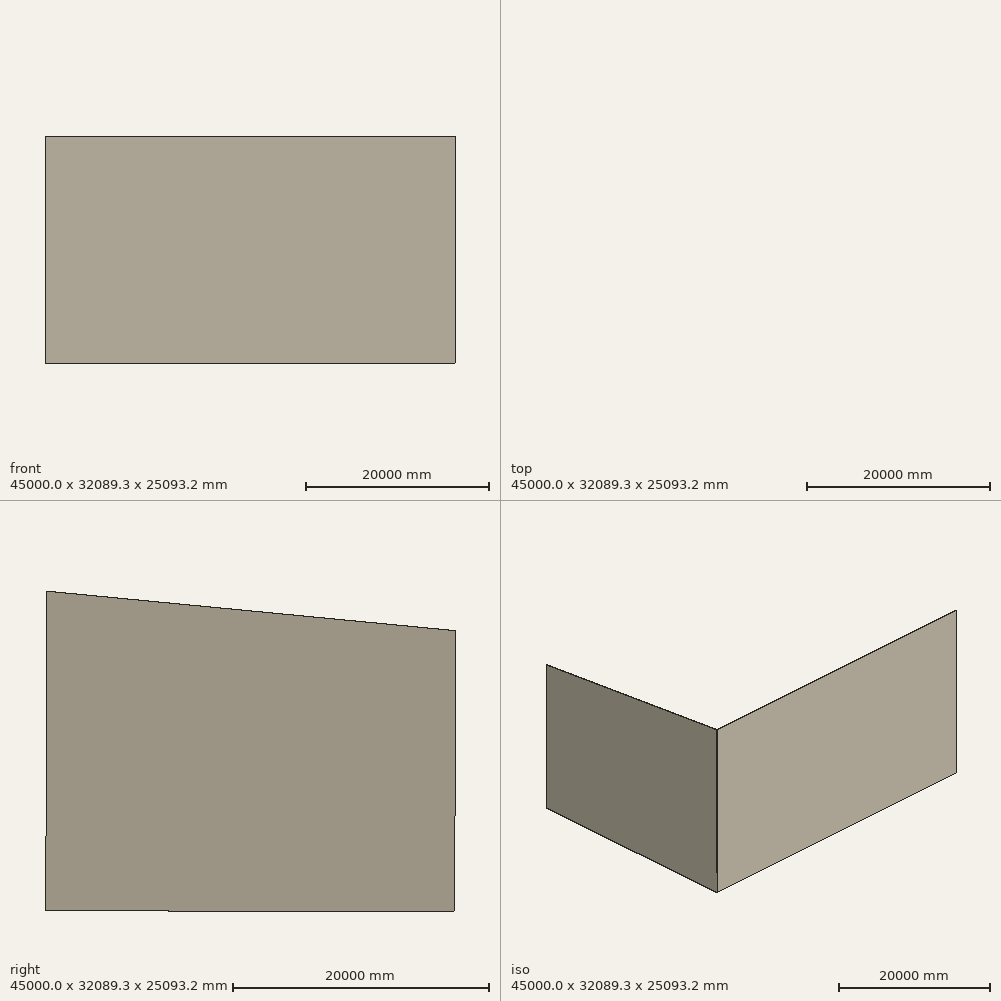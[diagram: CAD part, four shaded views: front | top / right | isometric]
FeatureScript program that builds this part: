
annotation { "Feature Type Name" : "Feature", "Feature Type Description" : "" }
export const myFeature = defineFeature(function(context is Context, id is Id, definition is map)
    precondition{}
    {
        {
            var Q0;
            Q0=qCreatedBy(makeId("Front.planeOp"),FACE);
            var sketch = newSketch(context, id + "F0", { "sketchPlane" : qUnion([Q0])});
            skLineSegment(sketch, "E0.bottom", {"start": v(0, 0) * mm, "end": v(45000, 0) * mm});
            skLineSegment(sketch, "E0.top", {"start": v(0, 25000) * mm, "end": v(45000, 25000) * mm});
            skLineSegment(sketch, "E0.left", {"start": v(0, 0) * mm, "end": v(0, 25000) * mm});
            skLineSegment(sketch, "E0.right", {"start": v(45000, 0) * mm, "end": v(45000, 25000) * mm});
            skSolve(sketch);
        }
        {
            var Q0;
            Q0 = qSketchRegion(id + "F0", true);
            extrude(context, id + "F1", {"entities" : qUnion([Q0]), "depth" : 25.4 * mm, "offsetDistance" : 25.4 * mm});
        }
        {
            var Q0;
            Q0=qCreatedBy(makeId("Right.planeOp"),FACE);
            var sketch = newSketch(context, id + "F2", { "sketchPlane" : qUnion([Q0])});
            skLineSegment(sketch, "E1", {"start": v(0, 0) * mm, "end": v(31999.86, -93.2) * mm});
            skLineSegment(sketch, "E2", {"start": v(31999.86, -93.2) * mm, "end": v(32063.93, 21906.72) * mm});
            skLineSegment(sketch, "E3", {"start": v(32063.93, 21906.72) * mm, "end": v(72.8, 24999.9) * mm});
            skLineSegment(sketch, "E4", {"start": v(72.8, 24999.9) * mm, "end": v(0, 0) * mm});
            skSolve(sketch);
        }
        {
            var Q0;
            Q0=makeQuery(id+"F2.imprint","IMPRINT",FACE,{"disambiguationData":[TD([[makeQuery(id+"F2.imprint","IMPRINT",EDGE,{"derivedFrom":sQuery(id+"F2.wireOp",EDGE,"E1")}),1.0]])]});
            extrude(context, id + "F3", {"entities" : qUnion([Q0]), "depth" : 25 * mm, "offsetDistance" : 25 * mm});
        }
    });
